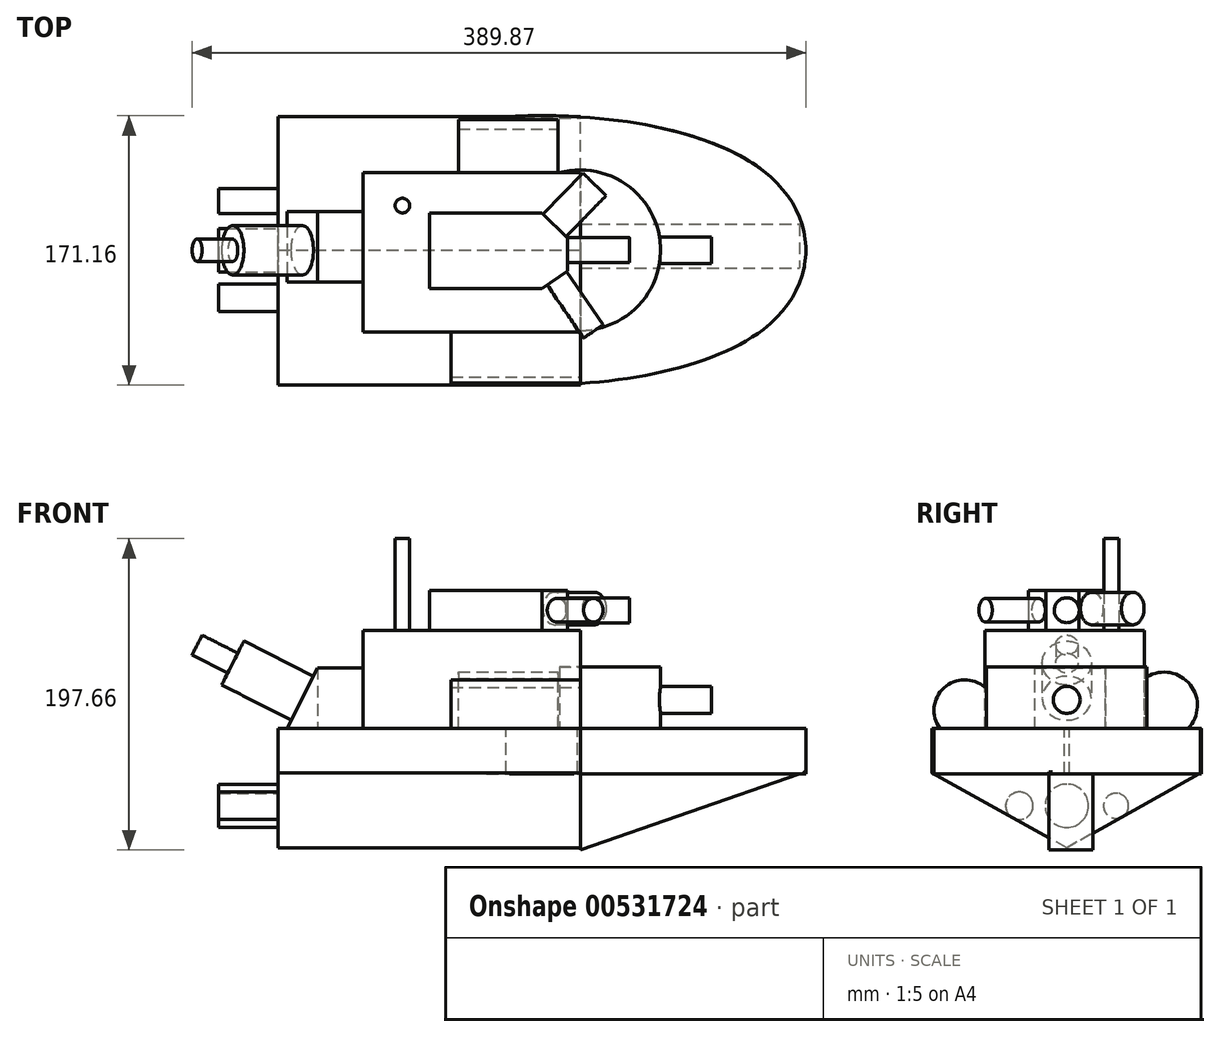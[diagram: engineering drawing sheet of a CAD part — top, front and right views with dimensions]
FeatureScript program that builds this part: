
annotation { "Feature Type Name" : "Feature", "Feature Type Description" : "" }
export const myFeature = defineFeature(function(context is Context, id is Id, definition is map)
    precondition{}
    {
        {
            var Q0;
            Q0=qCreatedBy(makeId("Top.planeOp"),FACE);
            var sketch = newSketch(context, id + "F0", { "sketchPlane" : qUnion([Q0])});
            skLineSegment(sketch, "E0.bottom", {"start": v(116.28, 50.42) * mm, "end": v(-165.04, 50.42) * mm});
            skLineSegment(sketch, "E0.top", {"start": v(116.28, -50.2) * mm, "end": v(-165.04, -50.2) * mm});
            skLineSegment(sketch, "E0.left", {"start": v(116.28, 50.42) * mm, "end": v(116.28, -50.2) * mm});
            skLineSegment(sketch, "E0.right", {"start": v(-165.04, 50.42) * mm, "end": v(-165.04, -50.2) * mm});
            skFitSpline(sketch, "E1", {"points": [v(-165.04, 50.42) * mm, v(116.28, 50.42) * mm, v(116.28, -50.2) * mm, v(-165.04, -50.2) * mm, v(-165.04, 50.42) * mm]});
            skSolve(sketch);
        }
        {
            var Q0;
            Q0 = qSketchRegion(id + "F0", true);
            extrude(context, id + "F1", {"entities" : qUnion([Q0]), "oppositeDirection" : true, "depth" : 28.7 * mm, "offsetDistance" : 25.4 * mm});
        }
        {
            var Q0;
            Q0=qCreatedBy(makeId("Right.planeOp"),FACE);
            var sketch = newSketch(context, id + "F2", { "sketchPlane" : qUnion([Q0])});
            skLineSegment(sketch, "E2", {"start": v(84.83, 0) * mm, "end": v(84.83, -28.18) * mm});
            skLineSegment(sketch, "E3", {"start": v(84.83, -28.18) * mm, "end": v(0, -75.76) * mm});
            skLineSegment(sketch, "E4", {"start": v(0, -75.76) * mm, "end": v(-85.67, -28.18) * mm});
            skLineSegment(sketch, "E5", {"start": v(-85.67, -28.18) * mm, "end": v(-85.67, 0) * mm});
            skLineSegment(sketch, "E6", {"start": v(-85.67, 0) * mm, "end": v(84.83, 0) * mm});
            skSolve(sketch);
        }
        {
            var Q0;
            Q0 = qSketchRegion(id + "F2", true);
            extrude(context, id + "F3", {"entities" : qUnion([Q0]), "operationType" : NewBodyOperationType.ADD, "oppositeDirection" : true, "depth" : 192.02 * mm, "offsetDistance" : 25.4 * mm});
        }
        {
            var Q0;
            Q0=qCreatedBy(makeId("Front.planeOp"),FACE);
            var sketch = newSketch(context, id + "F4", { "sketchPlane" : qUnion([Q0])});
            skLineSegment(sketch, "E7", {"start": v(0, -77.01) * mm, "end": v(142.5, -27.59) * mm});
            skLineSegment(sketch, "E8", {"start": v(142.5, -27.59) * mm, "end": v(0, -27.59) * mm});
            skLineSegment(sketch, "E9", {"start": v(0, -27.59) * mm, "end": v(0, -77.01) * mm});
            skSolve(sketch);
        }
        {
            var Q0;
            Q0 = qSketchRegion(id + "F4", true);
            extrude(context, id + "F5", {"entities" : qUnion([Q0]), "operationType" : NewBodyOperationType.ADD, "depth" : 11.18 * mm, "offsetDistance" : 25.4 * mm});
        }
        {
            var Q0;
            Q0=makeQuery(id+"F5.opExtrude","CAP_FACE",FACE,{"disambiguationData":[OSD([sQuery(id+"F4.wireOp",EDGE,"E7"),sQuery(id+"F4.wireOp",EDGE,"E8"),sQuery(id+"F4.wireOp",EDGE,"E9")])],"isStart":true});
            extrude(context, id + "F6", {"entities" : qUnion([Q0]), "operationType" : NewBodyOperationType.ADD, "depth" : 16.5 * mm, "offsetDistance" : 25.4 * mm});
        }
        {
            var Q0;
            Q0=qCreatedBy(makeId("Top.planeOp"),FACE);
            var sketch = newSketch(context, id + "F7", { "sketchPlane" : qUnion([Q0])});
            skCircle(sketch, "E10", {"center": v(0, 0) * mm, "radius": 50.98 * mm});
            skSolve(sketch);
        }
        {
            var Q0;
            Q0=makeQuery(id+"F7.imprint","IMPRINT",FACE,{"disambiguationData":[TD([[makeQuery(id+"F7.imprint","IMPRINT",EDGE,{"derivedFrom":sQuery(id+"F7.wireOp",EDGE,"E10")}),1.0]])]});
            extrude(context, id + "F8", {"entities" : qUnion([Q0]), "operationType" : NewBodyOperationType.ADD, "depth" : 39.12 * mm, "offsetDistance" : 25.4 * mm});
        }
        {
            var Q0;
            Q0=qCreatedBy(makeId("Top.planeOp"),FACE);
            var sketch = newSketch(context, id + "F9", { "sketchPlane" : qUnion([Q0])});
            skLineSegment(sketch, "E11.bottom", {"start": v(0, -51.98) * mm, "end": v(-138.06, -51.98) * mm});
            skLineSegment(sketch, "E11.top", {"start": v(0, 49.2) * mm, "end": v(-138.06, 49.2) * mm});
            skLineSegment(sketch, "E11.left", {"start": v(0, -51.98) * mm, "end": v(0, 49.2) * mm});
            skLineSegment(sketch, "E11.right", {"start": v(-138.06, -51.98) * mm, "end": v(-138.06, 49.2) * mm});
            skSolve(sketch);
        }
        {
            var Q0;
            Q0 = qSketchRegion(id + "F9", true);
            extrude(context, id + "F10", {"entities" : qUnion([Q0]), "operationType" : NewBodyOperationType.ADD, "depth" : 62.48 * mm, "offsetDistance" : 25.4 * mm});
        }
        {
            var Q0;
            Q0=qCreatedBy(makeId("Right.planeOp"),FACE);
            var sketch = newSketch(context, id + "F11", { "sketchPlane" : qUnion([Q0])});
            skCircle(sketch, "E12", {"center": v(0, 18.24) * mm, "radius": 8.54 * mm});
            skSolve(sketch);
        }
        {
            var Q0;
            Q0 = qSketchRegion(id + "F11", true);
            extrude(context, id + "F12", {"entities" : qUnion([Q0]), "operationType" : NewBodyOperationType.ADD, "depth" : 83.31 * mm, "offsetDistance" : 25.4 * mm});
        }
        {
            var Q0;
            Q0=qCreatedBy(makeId("Top.planeOp"),FACE);
            var sketch = newSketch(context, id + "F13", { "sketchPlane" : qUnion([Q0])});
            skLineSegment(sketch, "E13.bottom", {"start": v(-14.18, 49.16) * mm, "end": v(-75.79, 49.16) * mm});
            skLineSegment(sketch, "E13.top", {"start": v(-14.18, 74.83) * mm, "end": v(-75.79, 74.83) * mm});
            skLineSegment(sketch, "E13.left", {"start": v(-14.18, 49.16) * mm, "end": v(-14.18, 74.83) * mm});
            skLineSegment(sketch, "E13.right", {"start": v(-75.79, 49.16) * mm, "end": v(-75.79, 74.83) * mm});
            skSolve(sketch);
        }
        {
            var Q0;
            Q0 = qSketchRegion(id + "F13", true);
            extrude(context, id + "F14", {"entities" : qUnion([Q0]), "operationType" : NewBodyOperationType.ADD, "depth" : 29.46 * mm, "offsetDistance" : 25.4 * mm});
        }
        {
            var Q0;
            Q0=qCreatedBy(makeId("Top.planeOp"),FACE);
            var sketch = newSketch(context, id + "F15", { "sketchPlane" : qUnion([Q0])});
            skLineSegment(sketch, "E14.bottom", {"start": v(0, -54) * mm, "end": v(-38.11, -54) * mm});
            skLineSegment(sketch, "E14.top", {"start": v(0, -76.8) * mm, "end": v(-38.11, -76.8) * mm});
            skLineSegment(sketch, "E14.left", {"start": v(0, -54) * mm, "end": v(0, -76.8) * mm});
            skLineSegment(sketch, "E14.right", {"start": v(-38.11, -54) * mm, "end": v(-38.11, -76.8) * mm});
            skSolve(sketch);
        }
        {
            var Q0;
            Q0 = qSketchRegion(id + "F15", true);
            extrude(context, id + "F16", {"entities" : qUnion([Q0]), "operationType" : NewBodyOperationType.ADD, "depth" : 25.4 * mm, "offsetDistance" : 25.4 * mm});
        }
        {
            var Q0;
            Q0=makeQuery(id+"F14.opExtrude","SWEPT_FACE",FACE,{"disambiguationData":[OSD([sQuery(id+"F13.wireOp",EDGE,"E13.left")])]});
            var sketch = newSketch(context, id + "F17", { "sketchPlane" : qUnion([Q0])});
            skCircle(sketch, "E15", {"center": v(61.83, 14.73) * mm, "radius": 21.15 * mm});
            skPoint(sketch, "E15.centerSnap0", {"position": v(49.2, 14.73) * mm});
            skSolve(sketch);
        }
        {
            var Q0;
            Q0 = qSketchRegion(id + "F17", true);
            extrude(context, id + "F18", {"entities" : qUnion([Q0]), "operationType" : NewBodyOperationType.ADD, "oppositeDirection" : true, "depth" : 63.25 * mm, "offsetDistance" : 25.4 * mm});
        }
        {
            var Q0;
            Q0=makeQuery(id+"F16.opExtrude","SWEPT_FACE",FACE,{"disambiguationData":[OSD([sQuery(id+"F15.wireOp",EDGE,"E14.left")])]});
            var sketch = newSketch(context, id + "F19", { "sketchPlane" : qUnion([Q0])});
            skCircle(sketch, "E16", {"center": v(-64.76, 11.4) * mm, "radius": 19.56 * mm});
            skSolve(sketch);
        }
        {
            var Q0;
            Q0 = qSketchRegion(id + "F19", true);
            extrude(context, id + "F20", {"entities" : qUnion([Q0]), "operationType" : NewBodyOperationType.ADD, "oppositeDirection" : true, "depth" : 82.04 * mm, "offsetDistance" : 25.4 * mm});
        }
        {
            var Q0;
            Q0=makeQuery(id+"F10.opExtrude","CAP_FACE",FACE,{"disambiguationData":[OSD([sQuery(id+"F9.wireOp",EDGE,"E11.bottom"),sQuery(id+"F9.wireOp",EDGE,"E11.top"),sQuery(id+"F9.wireOp",EDGE,"E11.left"),sQuery(id+"F9.wireOp",EDGE,"E11.right")])],"isStart":false});
            var sketch = newSketch(context, id + "F21", { "sketchPlane" : qUnion([Q0])});
            skLineSegment(sketch, "E17.bottom", {"start": v(-24.4, 23.74) * mm, "end": v(-95.67, 23.74) * mm});
            skLineSegment(sketch, "E17.top", {"start": v(-24.4, -24.35) * mm, "end": v(-95.67, -24.35) * mm});
            skLineSegment(sketch, "E17.left", {"start": v(-24.4, 23.74) * mm, "end": v(-24.4, -24.35) * mm});
            skLineSegment(sketch, "E17.right", {"start": v(-95.67, 23.74) * mm, "end": v(-95.67, -24.35) * mm});
            skLineSegment(sketch, "E18", {"start": v(-24.4, -24.35) * mm, "end": v(-8.08, -13.19) * mm});
            skLineSegment(sketch, "E19", {"start": v(-8.08, -13.19) * mm, "end": v(-8.08, 7.85) * mm});
            skLineSegment(sketch, "E20", {"start": v(-8.08, 7.85) * mm, "end": v(-24.4, 23.74) * mm});
            skSolve(sketch);
        }
        {
            var Q0;
            Q0 = qSketchRegion(id + "F21", true);
            extrude(context, id + "F22", {"entities" : qUnion([Q0]), "operationType" : NewBodyOperationType.ADD, "depth" : 25.4 * mm, "offsetDistance" : 25.4 * mm});
        }
        {
            var Q0;
            Q0=makeQuery(id+"F22.opExtrude","SWEPT_FACE",FACE,{"disambiguationData":[OSD([sQuery(id+"F21.wireOp",EDGE,"E19")])]});
            var sketch = newSketch(context, id + "F23", { "sketchPlane" : qUnion([Q0])});
            skCircle(sketch, "E21", {"center": v(0, 75.18) * mm, "radius": 7.92 * mm});
            skPoint(sketch, "E21.centerSnap0", {"position": v(7.85, 75.18) * mm});
            skSolve(sketch);
        }
        {
            var Q0;
            Q0 = qSketchRegion(id + "F23", true);
            extrude(context, id + "F24", {"entities" : qUnion([Q0]), "operationType" : NewBodyOperationType.ADD, "depth" : 39.37 * mm, "offsetDistance" : 25.4 * mm});
        }
        {
            var Q0;
            Q0=makeQuery(id+"F22.opExtrude","SWEPT_FACE",FACE,{"disambiguationData":[OSD([sQuery(id+"F21.wireOp",EDGE,"E18")])]});
            var sketch = newSketch(context, id + "F25", { "sketchPlane" : qUnion([Q0])});
            skCircle(sketch, "E22", {"center": v(-22.28, 75.18) * mm, "radius": 7.52 * mm});
            skPoint(sketch, "E22.centerSnap0", {"position": v(-33.89, 75.18) * mm});
            skSolve(sketch);
        }
        {
            var Q0;
            Q0 = qSketchRegion(id + "F25", true);
            extrude(context, id + "F26", {"entities" : qUnion([Q0]), "operationType" : NewBodyOperationType.ADD, "depth" : 40.9 * mm, "offsetDistance" : 25.4 * mm});
        }
        {
            var Q0;
            Q0=makeQuery(id+"F22.opExtrude","SWEPT_FACE",FACE,{"disambiguationData":[OSD([sQuery(id+"F21.wireOp",EDGE,"E20")])]});
            var sketch = newSketch(context, id + "F27", { "sketchPlane" : qUnion([Q0])});
            skCircle(sketch, "E23", {"center": v(22.82, 76.26) * mm, "radius": 10.31 * mm});
            skSolve(sketch);
        }
        {
            var Q0;
            Q0 = qSketchRegion(id + "F27", true);
            extrude(context, id + "F28", {"entities" : qUnion([Q0]), "operationType" : NewBodyOperationType.ADD, "depth" : 36.32 * mm, "offsetDistance" : 25.4 * mm});
        }
        {
            var Q0;
            Q0=makeQuery(id+"F10.opExtrude","SWEPT_FACE",FACE,{"disambiguationData":[OSD([sQuery(id+"F9.wireOp",EDGE,"E11.right")])]});
            var sketch = newSketch(context, id + "F29", { "sketchPlane" : qUnion([Q0])});
            skLineSegment(sketch, "E24", {"start": v(20.29, 38.64) * mm, "end": v(-24.43, 38.64) * mm});
            skLineSegment(sketch, "E25", {"start": v(-24.43, 38.64) * mm, "end": v(-24.43, 0) * mm});
            skLineSegment(sketch, "E26", {"start": v(-24.43, 0) * mm, "end": v(20.29, 0) * mm});
            skLineSegment(sketch, "E27", {"start": v(20.29, 0) * mm, "end": v(20.29, 38.64) * mm});
            skSolve(sketch);
        }
        {
            var Q0;
            Q0=makeQuery(id+"F29.imprint","IMPRINT",FACE,{"disambiguationData":[TD([[makeQuery(id+"F29.imprint","IMPRINT",EDGE,{"derivedFrom":sQuery(id+"F29.wireOp",EDGE,"E24")}),1.0]])]});
            extrude(context, id + "F30", {"entities" : qUnion([Q0]), "operationType" : NewBodyOperationType.ADD, "depth" : 28.7 * mm, "offsetDistance" : 25.4 * mm});
        }
        {
            var Q0;
            Q0=makeQuery(id+"F30.opExtrude","SWEPT_FACE",FACE,{"disambiguationData":[OSD([sQuery(id+"F29.wireOp",EDGE,"E27")])]});
            var sketch = newSketch(context, id + "F31", { "sketchPlane" : qUnion([Q0])});
            skLineSegment(sketch, "E28", {"start": v(-166.76, 0) * mm, "end": v(-186.26, 0) * mm});
            skLineSegment(sketch, "E29", {"start": v(-186.26, 0) * mm, "end": v(-166.76, 38.64) * mm});
            skLineSegment(sketch, "E30", {"start": v(-166.76, 38.64) * mm, "end": v(-166.76, 0) * mm});
            skSolve(sketch);
        }
        {
            var Q0;
            Q0 = qSketchRegion(id + "F31", true);
            extrude(context, id + "F32", {"entities" : qUnion([Q0]), "operationType" : NewBodyOperationType.ADD, "oppositeDirection" : true, "depth" : 44.96 * mm, "offsetDistance" : 25.4 * mm});
        }
        {
            var Q0;
            Q0=makeQuery(id+"F32.opExtrude","SWEPT_FACE",FACE,{"disambiguationData":[OSD([sQuery(id+"F31.wireOp",EDGE,"E29")])]});
            var sketch = newSketch(context, id + "F33", { "sketchPlane" : qUnion([Q0])});
            skCircle(sketch, "E31", {"center": v(0, -62.29) * mm, "radius": 15.63 * mm});
            skPoint(sketch, "E31.centerSnap0", {"position": v(20.29, -62.29) * mm});
            skSolve(sketch);
        }
        {
            var Q0;
            Q0 = qSketchRegion(id + "F33", true);
            extrude(context, id + "F34", {"entities" : qUnion([Q0]), "operationType" : NewBodyOperationType.ADD, "depth" : 49.53 * mm, "offsetDistance" : 25.4 * mm});
        }
        {
            var Q0;
            Q0=makeQuery(id+"F34.opExtrude","CAP_FACE",FACE,{"disambiguationData":[OSD([sQuery(id+"F33.wireOp",EDGE,"E31")])],"isStart":false});
            var sketch = newSketch(context, id + "F35", { "sketchPlane" : qUnion([Q0])});
            skCircle(sketch, "E32", {"center": v(0, -62.29) * mm, "radius": 7.05 * mm});
            skSolve(sketch);
        }
        {
            var Q0;
            Q0 = qSketchRegion(id + "F35", true);
            extrude(context, id + "F36", {"entities" : qUnion([Q0]), "operationType" : NewBodyOperationType.ADD, "depth" : 25.4 * mm, "offsetDistance" : 25.4 * mm});
        }
        {
            var Q0;
            Q0=makeQuery(id+"F3.opExtrude","CAP_FACE",FACE,{"disambiguationData":[OSD([sQuery(id+"F2.wireOp",EDGE,"E2"),sQuery(id+"F2.wireOp",EDGE,"E3"),sQuery(id+"F2.wireOp",EDGE,"E4"),sQuery(id+"F2.wireOp",EDGE,"E5"),sQuery(id+"F2.wireOp",EDGE,"E6")])],"isStart":false});
            var sketch = newSketch(context, id + "F37", { "sketchPlane" : qUnion([Q0])});
            skCircle(sketch, "E33", {"center": v(0, -49.04) * mm, "radius": 13.75 * mm});
            skCircle(sketch, "E34", {"center": v(-31.33, -49.04) * mm, "radius": 7.97 * mm});
            skCircle(sketch, "E35", {"center": v(30.08, -49.04) * mm, "radius": 8.75 * mm});
            skSolve(sketch);
        }
        {
            var Q0;
            Q0 = qSketchRegion(id + "F37", true);
            extrude(context, id + "F38", {"entities" : qUnion([Q0]), "operationType" : NewBodyOperationType.ADD, "depth" : 37.6 * mm, "offsetDistance" : 25.4 * mm});
        }
        {
            var Q0;
            Q0=makeQuery(id+"F10.opExtrude","CAP_FACE",FACE,{"disambiguationData":[OSD([sQuery(id+"F9.wireOp",EDGE,"E11.bottom"),sQuery(id+"F9.wireOp",EDGE,"E11.top"),sQuery(id+"F9.wireOp",EDGE,"E11.left"),sQuery(id+"F9.wireOp",EDGE,"E11.right")])],"isStart":false});
            var sketch = newSketch(context, id + "F39", { "sketchPlane" : qUnion([Q0])});
            skCircle(sketch, "E36", {"center": v(-113, 28.38) * mm, "radius": 4.64 * mm});
            skSolve(sketch);
        }
        {
            var Q0;
            Q0 = qSketchRegion(id + "F39", true);
            extrude(context, id + "F40", {"entities" : qUnion([Q0]), "operationType" : NewBodyOperationType.ADD, "depth" : 58.17 * mm, "offsetDistance" : 25.4 * mm});
        }
    });
